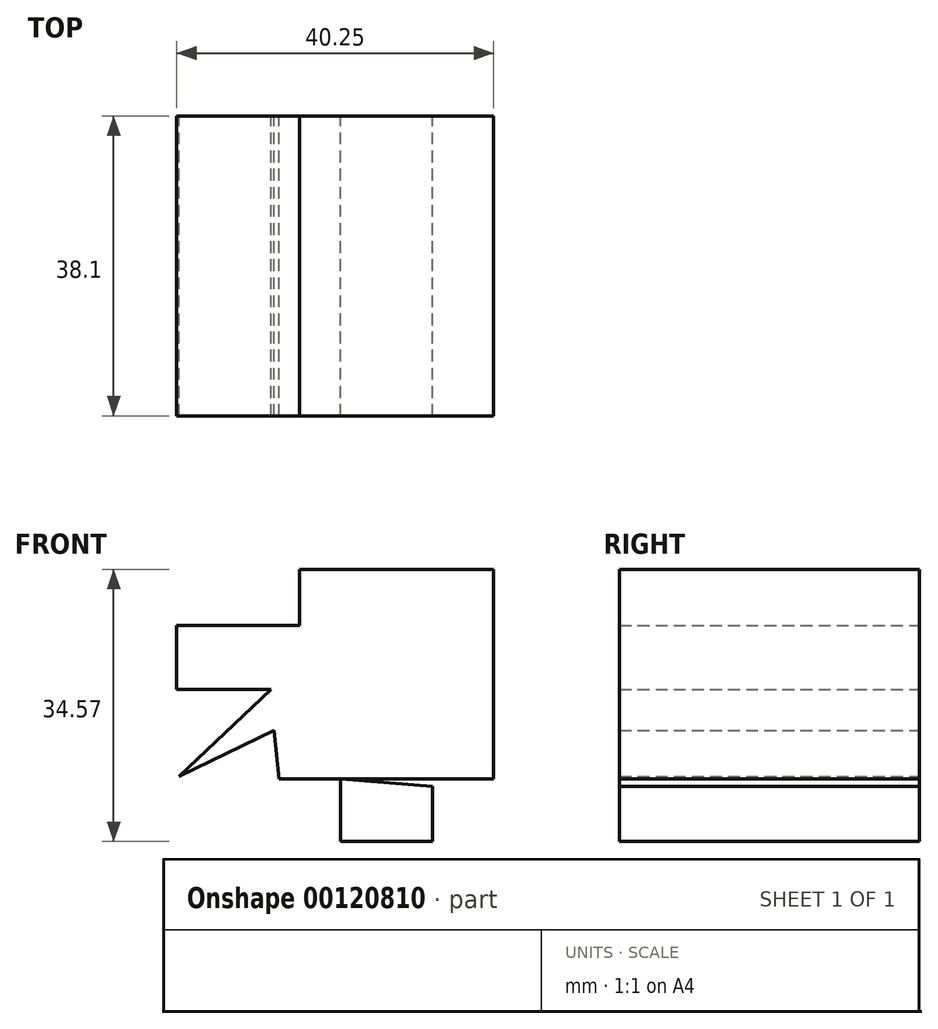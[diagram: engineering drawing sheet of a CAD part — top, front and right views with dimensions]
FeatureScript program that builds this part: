
annotation { "Feature Type Name" : "Feature", "Feature Type Description" : "" }
export const myFeature = defineFeature(function(context is Context, id is Id, definition is map)
    precondition{}
    {
        {
            var Q0;
            Q0=qCreatedBy(makeId("Front.planeOp"),FACE);
            var sketch = newSketch(context, id + "F0", { "sketchPlane" : qUnion([Q0])});
            skLineSegment(sketch, "E0.bottom", {"start": v(-19.48, 0) * mm, "end": v(20.12, 0) * mm});
            skLineSegment(sketch, "E0.top", {"start": v(-19.48, -56.32) * mm, "end": v(20.12, -56.32) * mm});
            skLineSegment(sketch, "E0.left", {"start": v(-19.48, 0) * mm, "end": v(-19.48, -56.32) * mm});
            skLineSegment(sketch, "E0.right", {"start": v(20.12, 0) * mm, "end": v(20.12, -56.32) * mm});
            skSolve(sketch);
        }
        {
            var Q0;
            Q0=qCreatedBy(makeId("Front.planeOp"),FACE);
            var sketch = newSketch(context, id + "F1", { "sketchPlane" : qUnion([Q0])});
            skLineSegment(sketch, "E1", {"start": v(-12.98, 7.95) * mm, "end": v(14.28, 7.95) * mm});
            skLineSegment(sketch, "E2", {"start": v(14.28, 7.95) * mm, "end": v(14.28, 34.57) * mm});
            skLineSegment(sketch, "E3", {"start": v(14.28, 34.57) * mm, "end": v(-10.39, 34.57) * mm});
            skLineSegment(sketch, "E4", {"start": v(-10.39, 34.57) * mm, "end": v(-10.39, 27.43) * mm});
            skLineSegment(sketch, "E5", {"start": v(-10.39, 27.43) * mm, "end": v(-25.97, 27.43) * mm});
            skLineSegment(sketch, "E6", {"start": v(-25.97, 27.43) * mm, "end": v(-25.97, 19.31) * mm});
            skLineSegment(sketch, "E7", {"start": v(-25.97, 19.31) * mm, "end": v(-13.96, 19.31) * mm});
            skLineSegment(sketch, "E8", {"start": v(-13.96, 19.31) * mm, "end": v(-25.64, 8.28) * mm});
            skLineSegment(sketch, "E9", {"start": v(-25.64, 8.28) * mm, "end": v(-13.63, 14.12) * mm});
            skLineSegment(sketch, "E10", {"start": v(-13.63, 14.12) * mm, "end": v(-12.98, 7.95) * mm});
            skSolve(sketch);
        }
        {
            var Q0;
            Q0 = qSketchRegion(id + "F1", true);
            extrude(context, id + "F2", {"entities" : qUnion([Q0]), "depth" : 38.1 * mm});
        }
        {
            var Q0;
            Q0=qCreatedBy(makeId("Front.planeOp"),FACE);
            var sketch = newSketch(context, id + "F3", { "sketchPlane" : qUnion([Q0])});
            skLineSegment(sketch, "E11", {"start": v(-5.2, 7.95) * mm, "end": v(-5.2, 0) * mm});
            skLineSegment(sketch, "E12", {"start": v(-5.2, 0) * mm, "end": v(6.5, 0) * mm});
            skLineSegment(sketch, "E13", {"start": v(6.5, 0) * mm, "end": v(6.5, 6.98) * mm});
            skLineSegment(sketch, "E14", {"start": v(6.5, 6.98) * mm, "end": v(-5.2, 7.95) * mm});
            skSolve(sketch);
        }
        {
            var Q0;
            Q0 = qSketchRegion(id + "F3", true);
            extrude(context, id + "F4", {"entities" : qUnion([Q0]), "operationType" : NewBodyOperationType.ADD, "depth" : 38.1 * mm});
        }
    });
